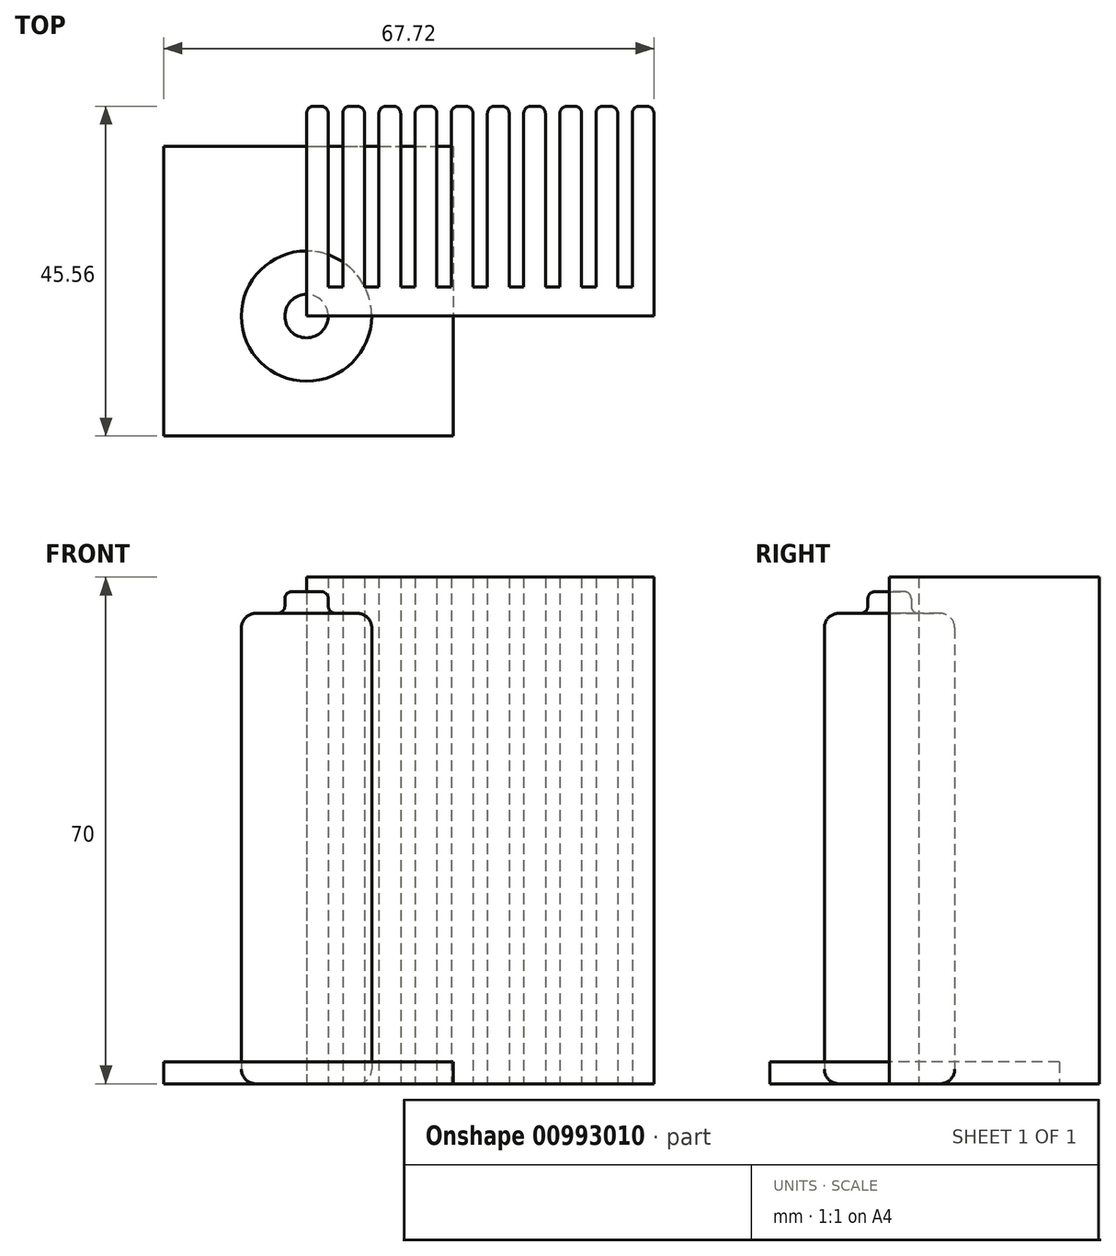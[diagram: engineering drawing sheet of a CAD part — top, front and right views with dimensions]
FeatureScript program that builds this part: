
annotation { "Feature Type Name" : "Feature", "Feature Type Description" : "" }
export const myFeature = defineFeature(function(context is Context, id is Id, definition is map)
    precondition{}
    {
        {
            var Q0;
            Q0=qCreatedBy(makeId("Top.planeOp"),FACE);
            var sketch = newSketch(context, id + "F0", { "sketchPlane" : qUnion([Q0])});
            skCircle(sketch, "E0", {"center": v(0, 0) * mm, "radius": 9 * mm});
            skSolve(sketch);
        }
        {
            var Q0;
            Q0 = qSketchRegion(id + "F0", true);
            extrude(context, id + "F1", {"entities" : qUnion([Q0]), "depth" : 65 * mm, "offsetDistance" : 25 * mm});
        }
        {
            var Q0;
            Q0=makeQuery(id+"F1.opExtrude","CAP_EDGE",EDGE,{"disambiguationData":[OSD([sQuery(id+"F0.wireOp",EDGE,"E0")])],"isStart":true});
            var Q1;
            Q1=makeQuery(id+"F1.opExtrude","CAP_EDGE",EDGE,{"disambiguationData":[OSD([sQuery(id+"F0.wireOp",EDGE,"E0")])],"isStart":false});
            fillet(context, id + "F2", {"entities" : qUnion([Q0, Q1]), "radius" : 2 * mm, "tangentPropagation" : true, "allowEdgeOverflow" : false});
        }
        {
            var Q0;
            Q0=makeQuery(id+"F1.opExtrude","CAP_FACE",FACE,{"disambiguationData":[OSD([sQuery(id+"F0.wireOp",EDGE,"E0")])],"isStart":false});
            var sketch = newSketch(context, id + "F3", { "sketchPlane" : qUnion([Q0])});
            skCircle(sketch, "E1", {"center": v(0, 0) * mm, "radius": 3 * mm});
            skSolve(sketch);
        }
        {
            var Q0;
            Q0=makeQuery(id+"F3.imprint","IMPRINT",FACE,{"disambiguationData":[TD([[makeQuery(id+"F3.imprint","IMPRINT",EDGE,{"derivedFrom":sQuery(id+"F3.wireOp",EDGE,"E1")}),1.0]])]});
            extrude(context, id + "F4", {"entities" : qUnion([Q0]), "operationType" : NewBodyOperationType.ADD, "depth" : 3 * mm, "offsetDistance" : 25 * mm});
        }
        {
            var Q0;
            Q0=makeQuery(id+"F4.opExtrude","SWEPT_FACE",FACE,{"disambiguationData":[OSD([sQuery(id+"F3.wireOp",EDGE,"E1")])]});
            var Q1;
            Q1=makeQuery(id+"F4.opExtrude","CAP_FACE",FACE,{"disambiguationData":[OSD([sQuery(id+"F3.wireOp",EDGE,"E1")])],"isStart":false});
            var Q2;
            Q2=makeQuery(id+"F1.opExtrude","CAP_FACE",FACE,{"disambiguationData":[OSD([sQuery(id+"F0.wireOp",EDGE,"E0")])],"isStart":false});
            fillet(context, id + "F5", {"entities" : qUnion([Q0, Q1, Q2]), "radius" : 1 * mm, "tangentPropagation" : true, "allowEdgeOverflow" : false});
        }
        {
            var Q0;
            Q0=qCreatedBy(makeId("Top.planeOp"),FACE);
            var sketch = newSketch(context, id + "F6", { "sketchPlane" : qUnion([Q0])});
            skLineSegment(sketch, "E2.bottom", {"start": v(-19.72, 23.44) * mm, "end": v(20.28, 23.44) * mm});
            skLineSegment(sketch, "E2.top", {"start": v(-19.72, -16.56) * mm, "end": v(20.28, -16.56) * mm});
            skLineSegment(sketch, "E2.left", {"start": v(-19.72, 23.44) * mm, "end": v(-19.72, -16.56) * mm});
            skLineSegment(sketch, "E2.right", {"start": v(20.28, 23.44) * mm, "end": v(20.28, -16.56) * mm});
            skSolve(sketch);
        }
        {
            var Q0;
            Q0=makeQuery(id+"F6.imprint","IMPRINT",FACE,{"disambiguationData":[TD([[makeQuery(id+"F6.imprint","IMPRINT",EDGE,{"derivedFrom":sQuery(id+"F6.wireOp",EDGE,"E2.bottom")}),-1.0]])]});
            extrude(context, id + "F7", {"entities" : qUnion([Q0]), "depth" : 3 * mm, "offsetDistance" : 25 * mm});
        }
        {
            var Q0;
            Q0=qCreatedBy(makeId("Top.planeOp"),FACE);
            var sketch = newSketch(context, id + "F8", { "sketchPlane" : qUnion([Q0])});
            skLineSegment(sketch, "E3.bottom", {"start": v(0, 0) * mm, "end": v(48, 0) * mm});
            skLineSegment(sketch, "E3.top", {"start": v(0, 4) * mm, "end": v(48, 4) * mm});
            skLineSegment(sketch, "E3.left", {"start": v(0, 0) * mm, "end": v(0, 4) * mm});
            skLineSegment(sketch, "E3.right", {"start": v(48, 0) * mm, "end": v(48, 4) * mm});
            skLineSegment(sketch, "E4.bottom", {"start": v(0, 4) * mm, "end": v(3, 4) * mm});
            skLineSegment(sketch, "E4.top", {"start": v(1, 29) * mm, "end": v(2, 29) * mm});
            skLineSegment(sketch, "E4.left", {"start": v(0, 4) * mm, "end": v(0, 28) * mm});
            skLineSegment(sketch, "E4.right", {"start": v(3, 4) * mm, "end": v(3, 28) * mm});
            skPoint(sketch, "E5.visualSharp", {"position": v(0, 29) * mm});
            skArc(sketch, "E5.filletArc", {"start": v(1, 29) * mm, "mid": v(0.3, 28.7) * mm, "end": v(0, 28) * mm});
            skPoint(sketch, "E6.visualSharp", {"position": v(3, 29) * mm});
            skArc(sketch, "E6.filletArc", {"start": v(3, 28) * mm, "mid": v(2.7, 28.7) * mm, "end": v(2, 29) * mm});
            skLineSegment(sketch, "E7.1.0.0", {"start": v(8, 4) * mm, "end": v(8, 28) * mm});
            skLineSegment(sketch, "E7.1.0.1", {"start": v(5, 4) * mm, "end": v(5, 28) * mm});
            skLineSegment(sketch, "E7.1.0.2", {"start": v(5, 4) * mm, "end": v(8, 4) * mm});
            skArc(sketch, "E7.1.0.3", {"start": v(6, 29) * mm, "mid": v(5.3, 28.7) * mm, "end": v(5, 28) * mm});
            skLineSegment(sketch, "E7.1.0.4", {"start": v(6, 29) * mm, "end": v(7, 29) * mm});
            skArc(sketch, "E7.1.0.5", {"start": v(8, 28) * mm, "mid": v(7.7, 28.7) * mm, "end": v(7, 29) * mm});
            skLineSegment(sketch, "E7.2.0.0", {"start": v(13, 4) * mm, "end": v(13, 28) * mm});
            skLineSegment(sketch, "E7.2.0.1", {"start": v(10, 4) * mm, "end": v(10, 28) * mm});
            skLineSegment(sketch, "E7.2.0.2", {"start": v(10, 4) * mm, "end": v(13, 4) * mm});
            skArc(sketch, "E7.2.0.3", {"start": v(11, 29) * mm, "mid": v(10.3, 28.7) * mm, "end": v(10, 28) * mm});
            skLineSegment(sketch, "E7.2.0.4", {"start": v(11, 29) * mm, "end": v(12, 29) * mm});
            skArc(sketch, "E7.2.0.5", {"start": v(13, 28) * mm, "mid": v(12.7, 28.7) * mm, "end": v(12, 29) * mm});
            skLineSegment(sketch, "E7.3.0.0", {"start": v(18, 4) * mm, "end": v(18, 28) * mm});
            skLineSegment(sketch, "E7.3.0.1", {"start": v(15, 4) * mm, "end": v(15, 28) * mm});
            skLineSegment(sketch, "E7.3.0.2", {"start": v(15, 4) * mm, "end": v(18, 4) * mm});
            skArc(sketch, "E7.3.0.3", {"start": v(16, 29) * mm, "mid": v(15.3, 28.7) * mm, "end": v(15, 28) * mm});
            skLineSegment(sketch, "E7.3.0.4", {"start": v(16, 29) * mm, "end": v(17, 29) * mm});
            skArc(sketch, "E7.3.0.5", {"start": v(18, 28) * mm, "mid": v(17.7, 28.7) * mm, "end": v(17, 29) * mm});
            skLineSegment(sketch, "E7.4.0.0", {"start": v(23, 4) * mm, "end": v(23, 28) * mm});
            skLineSegment(sketch, "E7.4.0.1", {"start": v(20, 4) * mm, "end": v(20, 28) * mm});
            skLineSegment(sketch, "E7.4.0.2", {"start": v(20, 4) * mm, "end": v(23, 4) * mm});
            skArc(sketch, "E7.4.0.3", {"start": v(21, 29) * mm, "mid": v(20.3, 28.7) * mm, "end": v(20, 28) * mm});
            skLineSegment(sketch, "E7.4.0.4", {"start": v(21, 29) * mm, "end": v(22, 29) * mm});
            skArc(sketch, "E7.4.0.5", {"start": v(23, 28) * mm, "mid": v(22.7, 28.7) * mm, "end": v(22, 29) * mm});
            skLineSegment(sketch, "E7.5.0.0", {"start": v(28, 4) * mm, "end": v(28, 28) * mm});
            skLineSegment(sketch, "E7.5.0.1", {"start": v(25, 4) * mm, "end": v(25, 28) * mm});
            skLineSegment(sketch, "E7.5.0.2", {"start": v(25, 4) * mm, "end": v(28, 4) * mm});
            skArc(sketch, "E7.5.0.3", {"start": v(26, 29) * mm, "mid": v(25.3, 28.7) * mm, "end": v(25, 28) * mm});
            skLineSegment(sketch, "E7.5.0.4", {"start": v(26, 29) * mm, "end": v(27, 29) * mm});
            skArc(sketch, "E7.5.0.5", {"start": v(28, 28) * mm, "mid": v(27.7, 28.7) * mm, "end": v(27, 29) * mm});
            skLineSegment(sketch, "E7.6.0.0", {"start": v(33, 4) * mm, "end": v(33, 28) * mm});
            skLineSegment(sketch, "E7.6.0.1", {"start": v(30, 4) * mm, "end": v(30, 28) * mm});
            skLineSegment(sketch, "E7.6.0.2", {"start": v(30, 4) * mm, "end": v(33, 4) * mm});
            skArc(sketch, "E7.6.0.3", {"start": v(31, 29) * mm, "mid": v(30.3, 28.7) * mm, "end": v(30, 28) * mm});
            skLineSegment(sketch, "E7.6.0.4", {"start": v(31, 29) * mm, "end": v(32, 29) * mm});
            skArc(sketch, "E7.6.0.5", {"start": v(33, 28) * mm, "mid": v(32.7, 28.7) * mm, "end": v(32, 29) * mm});
            skLineSegment(sketch, "E7.7.0.0", {"start": v(38, 4) * mm, "end": v(38, 28) * mm});
            skLineSegment(sketch, "E7.7.0.1", {"start": v(35, 4) * mm, "end": v(35, 28) * mm});
            skLineSegment(sketch, "E7.7.0.2", {"start": v(35, 4) * mm, "end": v(38, 4) * mm});
            skArc(sketch, "E7.7.0.3", {"start": v(36, 29) * mm, "mid": v(35.3, 28.7) * mm, "end": v(35, 28) * mm});
            skLineSegment(sketch, "E7.7.0.4", {"start": v(36, 29) * mm, "end": v(37, 29) * mm});
            skArc(sketch, "E7.7.0.5", {"start": v(38, 28) * mm, "mid": v(37.7, 28.7) * mm, "end": v(37, 29) * mm});
            skLineSegment(sketch, "E7.8.0.0", {"start": v(43, 4) * mm, "end": v(43, 28) * mm});
            skLineSegment(sketch, "E7.8.0.1", {"start": v(40, 4) * mm, "end": v(40, 28) * mm});
            skLineSegment(sketch, "E7.8.0.2", {"start": v(40, 4) * mm, "end": v(43, 4) * mm});
            skArc(sketch, "E7.8.0.3", {"start": v(41, 29) * mm, "mid": v(40.3, 28.7) * mm, "end": v(40, 28) * mm});
            skLineSegment(sketch, "E7.8.0.4", {"start": v(41, 29) * mm, "end": v(42, 29) * mm});
            skArc(sketch, "E7.8.0.5", {"start": v(43, 28) * mm, "mid": v(42.7, 28.7) * mm, "end": v(42, 29) * mm});
            skLineSegment(sketch, "E7.9.0.0", {"start": v(48, 4) * mm, "end": v(48, 28) * mm});
            skLineSegment(sketch, "E7.9.0.1", {"start": v(45, 4) * mm, "end": v(45, 28) * mm});
            skLineSegment(sketch, "E7.9.0.2", {"start": v(45, 4) * mm, "end": v(48, 4) * mm});
            skArc(sketch, "E7.9.0.3", {"start": v(46, 29) * mm, "mid": v(45.3, 28.7) * mm, "end": v(45, 28) * mm});
            skLineSegment(sketch, "E7.9.0.4", {"start": v(46, 29) * mm, "end": v(47, 29) * mm});
            skArc(sketch, "E7.9.0.5", {"start": v(48, 28) * mm, "mid": v(47.7, 28.7) * mm, "end": v(47, 29) * mm});
            skLineSegment(sketch, "E7.direction1", {"start": v(3, 4) * mm, "end": v(8, 4) * mm, "construction": true});
            skSolve(sketch);
        }
        {
            var Q0;
            Q0=makeQuery(id+"F8.imprint","IMPRINT",FACE,{"disambiguationData":[TD([[makeQuery(id+"F8.imprint","IMPRINT",EDGE,{"derivedFrom":sQuery(id+"F8.wireOp",EDGE,"E3.bottom")}),1.0]])]});
            var Q1;
            {var subQ0=sQuery(id+"F8.wireOp",EDGE,"E7.1.0.0");Q1=makeQuery(id+"F8.imprint","IMPRINT",FACE,{"disambiguationData":[TD([[makeQuery(id+"F8.imprint","IMPRINT",EDGE,{"derivedFrom":subQ0}),1.0]])]});}
            var Q2;
            {var subQ0=sQuery(id+"F8.wireOp",EDGE,"E7.3.0.0");Q2=makeQuery(id+"F8.imprint","IMPRINT",FACE,{"disambiguationData":[TD([[makeQuery(id+"F8.imprint","IMPRINT",EDGE,{"derivedFrom":subQ0}),1.0]])]});}
            var Q3;
            {var subQ1=sQuery(id+"F8.wireOp",EDGE,"E7.4.0.0");Q3=makeQuery(id+"F8.imprint","IMPRINT",FACE,{"disambiguationData":[TD([[makeQuery(id+"F8.imprint","IMPRINT",EDGE,{"derivedFrom":subQ1}),1.0]])]});}
            var Q4;
            {var subQ0=sQuery(id+"F8.wireOp",EDGE,"E7.5.0.0");Q4=makeQuery(id+"F8.imprint","IMPRINT",FACE,{"disambiguationData":[TD([[makeQuery(id+"F8.imprint","IMPRINT",EDGE,{"derivedFrom":subQ0}),1.0]])]});}
            var Q5;
            {var subQ0=sQuery(id+"F8.wireOp",EDGE,"E7.6.0.0");Q5=makeQuery(id+"F8.imprint","IMPRINT",FACE,{"disambiguationData":[TD([[makeQuery(id+"F8.imprint","IMPRINT",EDGE,{"derivedFrom":subQ0}),1.0]])]});}
            var Q6;
            {var subQ1=sQuery(id+"F8.wireOp",EDGE,"E7.7.0.0");Q6=makeQuery(id+"F8.imprint","IMPRINT",FACE,{"disambiguationData":[TD([[makeQuery(id+"F8.imprint","IMPRINT",EDGE,{"derivedFrom":subQ1}),1.0]])]});}
            var Q7;
            {var subQ1=sQuery(id+"F8.wireOp",EDGE,"E7.8.0.0");Q7=makeQuery(id+"F8.imprint","IMPRINT",FACE,{"disambiguationData":[TD([[makeQuery(id+"F8.imprint","IMPRINT",EDGE,{"derivedFrom":subQ1}),1.0]])]});}
            var Q8;
            {var subQ1=sQuery(id+"F8.wireOp",EDGE,"E7.9.0.0");Q8=makeQuery(id+"F8.imprint","IMPRINT",FACE,{"disambiguationData":[TD([[makeQuery(id+"F8.imprint","IMPRINT",EDGE,{"derivedFrom":subQ1}),1.0]])]});}
            var Q9;
            {var subQ1=sQuery(id+"F8.wireOp",EDGE,"E7.2.0.0");Q9=makeQuery(id+"F8.imprint","IMPRINT",FACE,{"disambiguationData":[TD([[makeQuery(id+"F8.imprint","IMPRINT",EDGE,{"derivedFrom":subQ1}),1.0]])]});}
            var Q10;
            Q10=makeQuery(id+"F8.imprint","IMPRINT",FACE,{"disambiguationData":[TD([[makeQuery(id+"F8.imprint","IMPRINT",EDGE,{"derivedFrom":sQuery(id+"F8.wireOp",EDGE,"E4.top")}),-1.0]])]});
            var Q11;
            Q11=sQuery(id+"F8.wireOp",EDGE,"E3.bottom");
            var Q12;
            Q12=sQuery(id+"F8.wireOp",EDGE,"E3.top");
            var Q13;
            Q13=sQuery(id+"F8.wireOp",EDGE,"E3.left");
            var Q14;
            Q14=sQuery(id+"F8.wireOp",EDGE,"E3.right");
            var Q15;
            Q15=sQuery(id+"F8.wireOp",EDGE,"E4.bottom");
            var Q16;
            Q16=sQuery(id+"F8.wireOp",EDGE,"E4.top");
            var Q17;
            Q17=sQuery(id+"F8.wireOp",EDGE,"E4.left");
            var Q18;
            Q18=sQuery(id+"F8.wireOp",EDGE,"E4.right");
            var Q19;
            Q19=sQuery(id+"F8.wireOp",EDGE,"E5.filletArc");
            var Q20;
            Q20=sQuery(id+"F8.wireOp",EDGE,"E6.filletArc");
            var Q21;
            Q21=sQuery(id+"F8.wireOp",EDGE,"E7.1.0.0");
            var Q22;
            Q22=sQuery(id+"F8.wireOp",EDGE,"E7.1.0.1");
            var Q23;
            Q23=sQuery(id+"F8.wireOp",EDGE,"E7.1.0.2");
            var Q24;
            Q24=sQuery(id+"F8.wireOp",EDGE,"E7.1.0.3");
            var Q25;
            Q25=sQuery(id+"F8.wireOp",EDGE,"E7.1.0.4");
            var Q26;
            Q26=sQuery(id+"F8.wireOp",EDGE,"E7.1.0.5");
            var Q27;
            Q27=sQuery(id+"F8.wireOp",EDGE,"E7.2.0.0");
            var Q28;
            Q28=sQuery(id+"F8.wireOp",EDGE,"E7.2.0.1");
            var Q29;
            Q29=sQuery(id+"F8.wireOp",EDGE,"E7.2.0.3");
            var Q30;
            Q30=sQuery(id+"F8.wireOp",EDGE,"E7.2.0.4");
            var Q31;
            Q31=sQuery(id+"F8.wireOp",EDGE,"E7.2.0.5");
            var Q32;
            Q32=sQuery(id+"F8.wireOp",EDGE,"E7.3.0.0");
            var Q33;
            Q33=sQuery(id+"F8.wireOp",EDGE,"E7.3.0.1");
            var Q34;
            Q34=sQuery(id+"F8.wireOp",EDGE,"E7.3.0.2");
            var Q35;
            Q35=sQuery(id+"F8.wireOp",EDGE,"E7.3.0.3");
            var Q36;
            Q36=sQuery(id+"F8.wireOp",EDGE,"E7.3.0.4");
            var Q37;
            Q37=sQuery(id+"F8.wireOp",EDGE,"E7.3.0.5");
            var Q38;
            Q38=sQuery(id+"F8.wireOp",EDGE,"E7.4.0.0");
            var Q39;
            Q39=sQuery(id+"F8.wireOp",EDGE,"E7.4.0.1");
            var Q40;
            Q40=sQuery(id+"F8.wireOp",EDGE,"E7.4.0.2");
            var Q41;
            Q41=sQuery(id+"F8.wireOp",EDGE,"E7.4.0.3");
            var Q42;
            Q42=sQuery(id+"F8.wireOp",EDGE,"E7.4.0.4");
            var Q43;
            Q43=sQuery(id+"F8.wireOp",EDGE,"E7.4.0.5");
            var Q44;
            Q44=sQuery(id+"F8.wireOp",EDGE,"E7.5.0.0");
            var Q45;
            Q45=sQuery(id+"F8.wireOp",EDGE,"E7.5.0.1");
            var Q46;
            Q46=sQuery(id+"F8.wireOp",EDGE,"E7.5.0.2");
            var Q47;
            Q47=sQuery(id+"F8.wireOp",EDGE,"E7.5.0.3");
            var Q48;
            Q48=sQuery(id+"F8.wireOp",EDGE,"E7.5.0.4");
            var Q49;
            Q49=sQuery(id+"F8.wireOp",EDGE,"E7.5.0.5");
            var Q50;
            Q50=sQuery(id+"F8.wireOp",EDGE,"E7.6.0.0");
            var Q51;
            Q51=sQuery(id+"F8.wireOp",EDGE,"E7.6.0.1");
            var Q52;
            Q52=sQuery(id+"F8.wireOp",EDGE,"E7.6.0.2");
            var Q53;
            Q53=sQuery(id+"F8.wireOp",EDGE,"E7.6.0.3");
            var Q54;
            Q54=sQuery(id+"F8.wireOp",EDGE,"E7.6.0.4");
            var Q55;
            Q55=sQuery(id+"F8.wireOp",EDGE,"E7.6.0.5");
            var Q56;
            Q56=sQuery(id+"F8.wireOp",EDGE,"E7.7.0.0");
            var Q57;
            Q57=sQuery(id+"F8.wireOp",EDGE,"E7.7.0.1");
            var Q58;
            Q58=sQuery(id+"F8.wireOp",EDGE,"E7.7.0.2");
            var Q59;
            Q59=sQuery(id+"F8.wireOp",EDGE,"E7.7.0.3");
            var Q60;
            Q60=sQuery(id+"F8.wireOp",EDGE,"E7.7.0.4");
            var Q61;
            Q61=sQuery(id+"F8.wireOp",EDGE,"E7.7.0.5");
            var Q62;
            Q62=sQuery(id+"F8.wireOp",EDGE,"E7.8.0.0");
            var Q63;
            Q63=sQuery(id+"F8.wireOp",EDGE,"E7.8.0.1");
            var Q64;
            Q64=sQuery(id+"F8.wireOp",EDGE,"E7.8.0.2");
            var Q65;
            Q65=sQuery(id+"F8.wireOp",EDGE,"E7.8.0.3");
            var Q66;
            Q66=sQuery(id+"F8.wireOp",EDGE,"E7.8.0.4");
            var Q67;
            Q67=sQuery(id+"F8.wireOp",EDGE,"E7.8.0.5");
            var Q68;
            Q68=sQuery(id+"F8.wireOp",EDGE,"E7.9.0.0");
            var Q69;
            Q69=sQuery(id+"F8.wireOp",EDGE,"E7.9.0.1");
            var Q70;
            Q70=sQuery(id+"F8.wireOp",EDGE,"E7.9.0.2");
            var Q71;
            Q71=sQuery(id+"F8.wireOp",EDGE,"E7.9.0.3");
            var Q72;
            Q72=sQuery(id+"F8.wireOp",EDGE,"E7.9.0.4");
            var Q73;
            Q73=sQuery(id+"F8.wireOp",EDGE,"E7.9.0.5");
            extrude(context, id + "F9", {"entities" : qUnion([Q0, Q1, Q2, Q3, Q4, Q5, Q6, Q7, Q8, Q9, Q10]), "surfaceEntities" : qUnion([Q11, Q12, Q13, Q14, Q15, Q16, Q17, Q18, Q19, Q20, Q21, Q22, Q23, Q24, Q25, Q26, Q27, Q28, Q29, Q30, Q31, Q32, Q33, Q34, Q35, Q36, Q37, Q38, Q39, Q40, Q41, Q42, Q43, Q44, Q45, Q46, Q47, Q48, Q49, Q50, Q51, Q52, Q53, Q54, Q55, Q56, Q57, Q58, Q59, Q60, Q61, Q62, Q63, Q64, Q65, Q66, Q67, Q68, Q69, Q70, Q71, Q72, Q73]), "depth" : 70 * mm, "offsetDistance" : 25 * mm});
        }
    });
